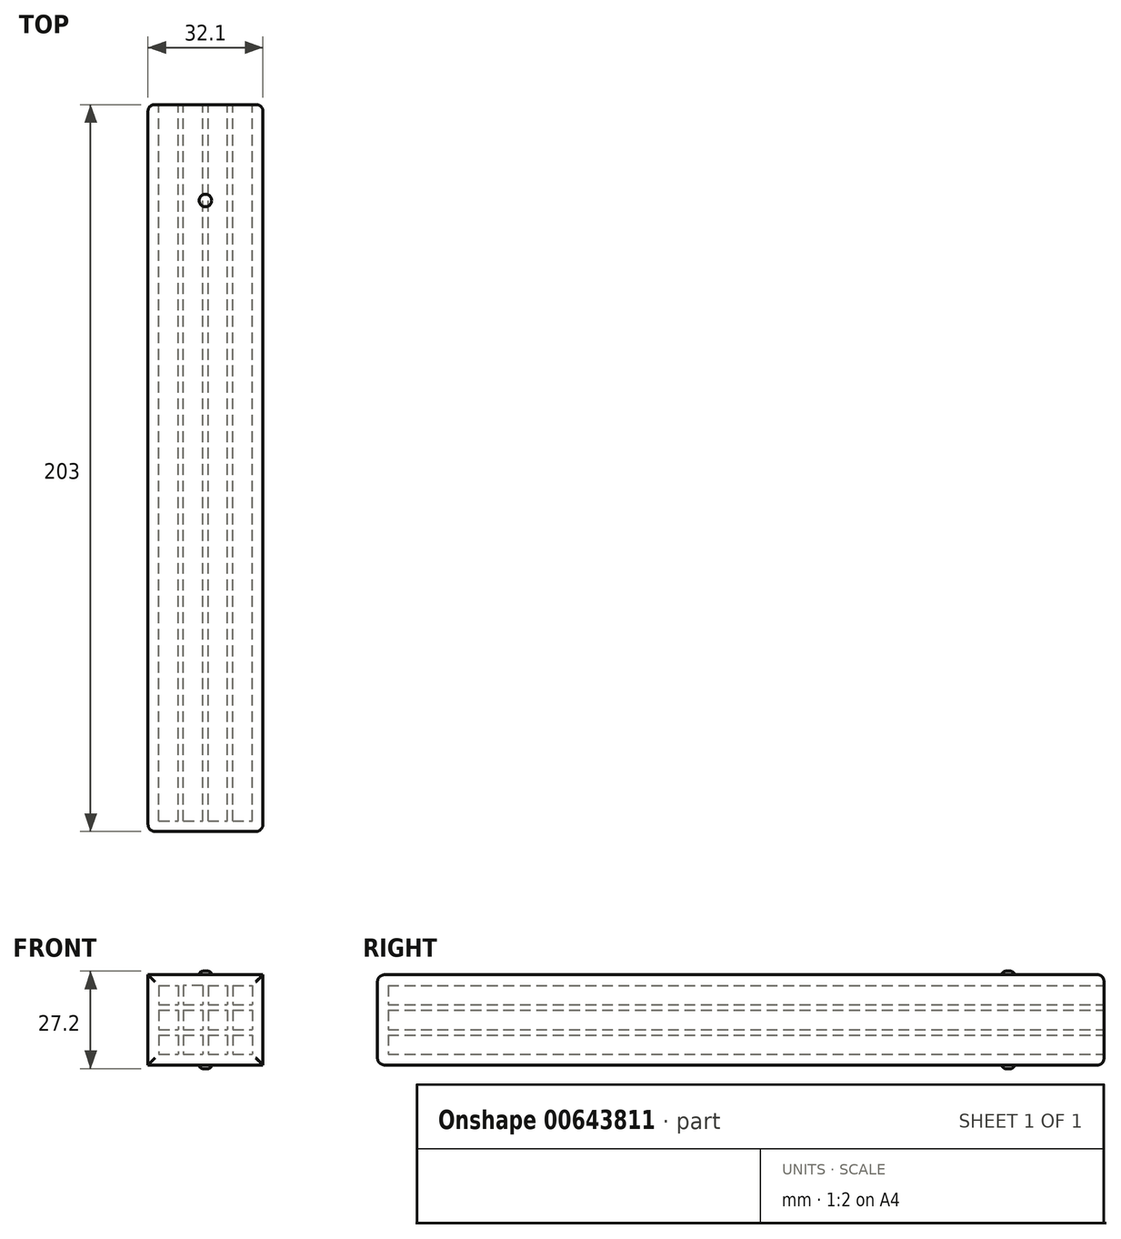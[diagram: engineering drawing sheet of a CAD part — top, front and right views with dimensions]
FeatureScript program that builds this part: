
annotation { "Feature Type Name" : "Feature", "Feature Type Description" : "" }
export const myFeature = defineFeature(function(context is Context, id is Id, definition is map)
    precondition{}
    {
        {
            var Q0;
            Q0=qCreatedBy(makeId("Front.planeOp"),FACE);
            var sketch = newSketch(context, id + "F0", { "sketchPlane" : qUnion([Q0])});
            skLineSegment(sketch, "E0.top", {"start": v(-16.76, 12.2) * mm, "end": v(15.34, 12.2) * mm});
            skLineSegment(sketch, "E0.left", {"start": v(-16.76, -13) * mm, "end": v(-16.76, 12.2) * mm});
            skLineSegment(sketch, "E1.0", {"start": v(-13.76, 9.2) * mm, "end": v(-8.01, 9.2) * mm});
            skLineSegment(sketch, "E2.bottom", {"start": v(-13.76, 9.2) * mm, "end": v(-8.36, 9.2) * mm});
            skLineSegment(sketch, "E2.left", {"start": v(-4.86, 32.02) * mm, "end": v(-4.86, 32.02) * mm});
            skLineSegment(sketch, "E3.bottom", {"start": v(-1.46, 9.2) * mm, "end": v(-6.86, 9.2) * mm});
            skLineSegment(sketch, "E4.left", {"start": v(-13.76, 0.75) * mm, "end": v(-13.76, -3.1) * mm});
            skLineSegment(sketch, "E5.left", {"start": v(-13.76, 9.2) * mm, "end": v(-13.76, 3.8) * mm});
            skLineSegment(sketch, "E6", {"start": v(-8.36, 9.2) * mm, "end": v(-8.36, 3.8) * mm});
            skLineSegment(sketch, "E7", {"start": v(-6.86, 9.2) * mm, "end": v(-6.86, 3.8) * mm});
            skLineSegment(sketch, "E8", {"start": v(-1.46, 9.2) * mm, "end": v(-1.46, 3.8) * mm});
            skLineSegment(sketch, "E9", {"start": v(0.04, 9.2) * mm, "end": v(0.04, 3.8) * mm});
            skLineSegment(sketch, "E10", {"start": v(5.44, 9.2) * mm, "end": v(5.44, 3.8) * mm});
            skLineSegment(sketch, "E11", {"start": v(6.94, 9.2) * mm, "end": v(6.94, 3.8) * mm});
            skLineSegment(sketch, "E12", {"start": v(-13.76, 3.8) * mm, "end": v(-8.36, 3.8) * mm});
            skLineSegment(sketch, "E13", {"start": v(-13.76, 2.3) * mm, "end": v(-8.36, 2.3) * mm});
            skLineSegment(sketch, "E14", {"start": v(-13.76, -3.1) * mm, "end": v(-8.36, -3.1) * mm});
            skLineSegment(sketch, "E15", {"start": v(12.34, 9.2) * mm, "end": v(12.34, 3.8) * mm});
            skLineSegment(sketch, "E16", {"start": v(15.34, 12.2) * mm, "end": v(15.34, -13) * mm});
            skPoint(sketch, "E17.orphan", {"position": v(13.24, 9.2) * mm});
            skPoint(sketch, "E18.orphan", {"position": v(13.24, 3.8) * mm});
            skPoint(sketch, "E19.orphan", {"position": v(13.24, 2.3) * mm});
            skPoint(sketch, "E20.orphan", {"position": v(13.24, -2.88) * mm});
            skPoint(sketch, "E21.orphan", {"position": v(13.24, -9.45) * mm});
            skLineSegment(sketch, "E22.0", {"start": v(-13.76, -4.6) * mm, "end": v(-8.36, -4.6) * mm});
            skLineSegment(sketch, "E23.0", {"start": v(-13.76, -10) * mm, "end": v(-8.36, -10) * mm});
            skLineSegment(sketch, "E24.trimOffspring", {"start": v(6.94, -10) * mm, "end": v(12.34, -10) * mm});
            skLineSegment(sketch, "E25.trimOffspring", {"start": v(6.94, -4.6) * mm, "end": v(12.34, -4.6) * mm});
            skLineSegment(sketch, "E26.trimOffspring", {"start": v(5.44, -4.6) * mm, "end": v(5.44, -10) * mm});
            skLineSegment(sketch, "E27.trimOffspring", {"start": v(6.94, -3.1) * mm, "end": v(12.34, -3.1) * mm});
            skLineSegment(sketch, "E28.trimOffspring", {"start": v(6.94, -4.6) * mm, "end": v(6.94, -10) * mm});
            skLineSegment(sketch, "E29.trimOffspring", {"start": v(12.34, -4.6) * mm, "end": v(12.34, -10) * mm});
            skLineSegment(sketch, "E30.trimOffspring", {"start": v(12.34, 2.3) * mm, "end": v(12.34, -3.1) * mm});
            skLineSegment(sketch, "E31.trimOffspring", {"start": v(6.94, 2.3) * mm, "end": v(6.94, -3.1) * mm});
            skLineSegment(sketch, "E32.trimOffspring", {"start": v(5.44, 2.3) * mm, "end": v(5.44, -3.1) * mm});
            skLineSegment(sketch, "E33.trimOffspring", {"start": v(6.94, 3.8) * mm, "end": v(12.34, 3.8) * mm});
            skLineSegment(sketch, "E34.trimOffspring", {"start": v(6.94, 2.3) * mm, "end": v(12.34, 2.3) * mm});
            skLineSegment(sketch, "E35.trimOffspring", {"start": v(0.04, -10) * mm, "end": v(5.44, -10) * mm});
            skLineSegment(sketch, "E36.trimOffspring", {"start": v(-6.86, 9.2) * mm, "end": v(-1.46, 9.2) * mm});
            skLineSegment(sketch, "E37.trimOffspring", {"start": v(-6.86, 3.8) * mm, "end": v(-1.46, 3.8) * mm});
            skLineSegment(sketch, "E38.trimOffspring", {"start": v(-6.86, 2.3) * mm, "end": v(-1.46, 2.3) * mm});
            skLineSegment(sketch, "E39.trimOffspring", {"start": v(-8.36, 2.3) * mm, "end": v(-8.36, -3.1) * mm});
            skLineSegment(sketch, "E40.trimOffspring", {"start": v(-6.86, 2.3) * mm, "end": v(-6.86, -3.1) * mm});
            skLineSegment(sketch, "E41.trimOffspring", {"start": v(-13.76, 3.8) * mm, "end": v(-13.76, 9.2) * mm});
            skLineSegment(sketch, "E42.trimOffspring", {"start": v(-13.76, -4.6) * mm, "end": v(-13.76, -6.95) * mm});
            skLineSegment(sketch, "E43.trimOffspring", {"start": v(-8.36, -4.6) * mm, "end": v(-8.36, -10) * mm});
            skLineSegment(sketch, "E44.trimOffspring", {"start": v(-6.86, -3.1) * mm, "end": v(-1.46, -3.1) * mm});
            skLineSegment(sketch, "E45.trimOffspring", {"start": v(-6.86, -4.6) * mm, "end": v(-6.86, -10) * mm});
            skLineSegment(sketch, "E46.trimOffspring", {"start": v(-6.86, -4.6) * mm, "end": v(-1.46, -4.6) * mm});
            skLineSegment(sketch, "E47.trimOffspring", {"start": v(-1.46, -4.6) * mm, "end": v(-1.46, -10) * mm});
            skLineSegment(sketch, "E48.trimOffspring", {"start": v(0.04, -3.1) * mm, "end": v(5.44, -3.1) * mm});
            skLineSegment(sketch, "E49.trimOffspring", {"start": v(0.04, -4.6) * mm, "end": v(0.04, -10) * mm});
            skLineSegment(sketch, "E50.trimOffspring", {"start": v(0.04, -4.6) * mm, "end": v(5.44, -4.6) * mm});
            skLineSegment(sketch, "E51.trimOffspring", {"start": v(-6.86, -10) * mm, "end": v(-1.46, -10) * mm});
            skLineSegment(sketch, "E52.trimOffspring", {"start": v(-13.76, -10) * mm, "end": v(-13.76, 2.3) * mm});
            skLineSegment(sketch, "E53.trimOffspring", {"start": v(0.04, 2.3) * mm, "end": v(5.44, 2.3) * mm});
            skLineSegment(sketch, "E54.trimOffspring", {"start": v(0.04, 3.8) * mm, "end": v(5.44, 3.8) * mm});
            skLineSegment(sketch, "E55.trimOffspring", {"start": v(-1.46, 2.3) * mm, "end": v(-1.46, -3.1) * mm});
            skLineSegment(sketch, "E56.trimOffspring", {"start": v(0.04, 2.3) * mm, "end": v(0.04, -3.1) * mm});
            skPoint(sketch, "E57.orphan", {"position": v(-0.26, 9.2) * mm});
            skLineSegment(sketch, "E58.trimOffspring", {"start": v(0.04, 9.2) * mm, "end": v(5.44, 9.2) * mm});
            skLineSegment(sketch, "E59.trimOffspring", {"start": v(6.94, 9.2) * mm, "end": v(12.34, 9.2) * mm});
            skLineSegment(sketch, "E60", {"start": v(-16.76, -13) * mm, "end": v(15.34, -13) * mm});
            skSolve(sketch);
        }
        {
            var Q0;
            Q0=makeQuery(id+"F0.imprint","IMPRINT",FACE,{"disambiguationData":[TD([[makeQuery(id+"F0.imprint","IMPRINT",EDGE,{"derivedFrom":sQuery(id+"F0.wireOp",EDGE,"E0.top")}),-1.0]])]});
            extrude(context, id + "F1", {"entities" : qUnion([Q0]), "depth" : 200 * mm, "offsetDistance" : 25 * mm});
        }
        {
            var Q0;
            Q0=makeQuery(id+"F1.opExtrude","CAP_FACE",FACE,{"disambiguationData":[OSD([sQuery(id+"F0.wireOp",EDGE,"E0.top"),sQuery(id+"F0.wireOp",EDGE,"E0.left"),sQuery(id+"F0.wireOp",EDGE,"E1.0"),sQuery(id+"F0.wireOp",EDGE,"E6"),sQuery(id+"F0.wireOp",EDGE,"E7"),sQuery(id+"F0.wireOp",EDGE,"E8"),sQuery(id+"F0.wireOp",EDGE,"E9"),sQuery(id+"F0.wireOp",EDGE,"E10"),sQuery(id+"F0.wireOp",EDGE,"E11"),sQuery(id+"F0.wireOp",EDGE,"E12"),sQuery(id+"F0.wireOp",EDGE,"E13"),sQuery(id+"F0.wireOp",EDGE,"E14"),sQuery(id+"F0.wireOp",EDGE,"E15"),sQuery(id+"F0.wireOp",EDGE,"E16"),sQuery(id+"F0.wireOp",EDGE,"E22.0"),sQuery(id+"F0.wireOp",EDGE,"E23.0"),sQuery(id+"F0.wireOp",EDGE,"E24.trimOffspring"),sQuery(id+"F0.wireOp",EDGE,"E25.trimOffspring"),sQuery(id+"F0.wireOp",EDGE,"E26.trimOffspring"),sQuery(id+"F0.wireOp",EDGE,"E27.trimOffspring"),sQuery(id+"F0.wireOp",EDGE,"E28.trimOffspring"),sQuery(id+"F0.wireOp",EDGE,"E29.trimOffspring"),sQuery(id+"F0.wireOp",EDGE,"E30.trimOffspring"),sQuery(id+"F0.wireOp",EDGE,"E31.trimOffspring"),sQuery(id+"F0.wireOp",EDGE,"E32.trimOffspring"),sQuery(id+"F0.wireOp",EDGE,"E33.trimOffspring"),sQuery(id+"F0.wireOp",EDGE,"E34.trimOffspring"),sQuery(id+"F0.wireOp",EDGE,"E35.trimOffspring"),sQuery(id+"F0.wireOp",EDGE,"E36.trimOffspring"),sQuery(id+"F0.wireOp",EDGE,"E37.trimOffspring"),sQuery(id+"F0.wireOp",EDGE,"E38.trimOffspring"),sQuery(id+"F0.wireOp",EDGE,"E39.trimOffspring"),sQuery(id+"F0.wireOp",EDGE,"E40.trimOffspring"),sQuery(id+"F0.wireOp",EDGE,"E41.trimOffspring"),sQuery(id+"F0.wireOp",EDGE,"E43.trimOffspring"),sQuery(id+"F0.wireOp",EDGE,"E44.trimOffspring"),sQuery(id+"F0.wireOp",EDGE,"E45.trimOffspring"),sQuery(id+"F0.wireOp",EDGE,"E46.trimOffspring"),sQuery(id+"F0.wireOp",EDGE,"E47.trimOffspring"),sQuery(id+"F0.wireOp",EDGE,"E48.trimOffspring"),sQuery(id+"F0.wireOp",EDGE,"E49.trimOffspring"),sQuery(id+"F0.wireOp",EDGE,"E50.trimOffspring"),sQuery(id+"F0.wireOp",EDGE,"E51.trimOffspring"),sQuery(id+"F0.wireOp",EDGE,"E52.trimOffspring"),sQuery(id+"F0.wireOp",EDGE,"E53.trimOffspring"),sQuery(id+"F0.wireOp",EDGE,"E54.trimOffspring"),sQuery(id+"F0.wireOp",EDGE,"E55.trimOffspring"),sQuery(id+"F0.wireOp",EDGE,"E56.trimOffspring"),sQuery(id+"F0.wireOp",EDGE,"E58.trimOffspring"),sQuery(id+"F0.wireOp",EDGE,"E59.trimOffspring"),sQuery(id+"F0.wireOp",EDGE,"E60")])],"isStart":false});
            var sketch = newSketch(context, id + "F2", { "sketchPlane" : qUnion([Q0])});
            skSolve(sketch);
        }
        {
            var Q0;
            Q0=makeQuery(id+"F2.imprint","IMPRINT",FACE,{"disambiguationData":[TD([[makeQuery(id+"F2.imprint","IMPRINT",EDGE,{"derivedFrom":makeQuery(id+"F1.opExtrude","CAP_EDGE",EDGE,{"disambiguationData":[OSD([sQuery(id+"F0.wireOp",EDGE,"E0.top")])],"isStart":false})}),-1.0]])]});
            var sketch = newSketch(context, id + "F3", { "sketchPlane" : qUnion([Q0])});
            skPoint(sketch, "E61.0", {"position": v(-16.76, 12.2) * mm});
            skPoint(sketch, "E62.0", {"position": v(15.34, -13) * mm});
            skLineSegment(sketch, "E63.bottom", {"start": v(-16.76, 12.2) * mm, "end": v(15.34, 12.2) * mm});
            skLineSegment(sketch, "E63.top", {"start": v(-16.76, -13) * mm, "end": v(15.34, -13) * mm});
            skLineSegment(sketch, "E63.left", {"start": v(-16.76, 12.2) * mm, "end": v(-16.76, -13) * mm});
            skLineSegment(sketch, "E63.right", {"start": v(15.34, 12.2) * mm, "end": v(15.34, -13) * mm});
            skSolve(sketch);
        }
        {
            var Q0;
            Q0 = qSketchRegion(id + "F3", true);
            extrude(context, id + "F4", {"entities" : qUnion([Q0]), "operationType" : NewBodyOperationType.ADD, "depth" : 3 * mm, "offsetDistance" : 25 * mm});
        }
        {
            var Q0;
            Q0=makeQuery(id+"F4.opExtrude","CAP_EDGE",EDGE,{"disambiguationData":[OSD([sQuery(id+"F3.wireOp",EDGE,"E63.right")])],"isStart":false});
            var Q1;
            Q1=makeQuery(id+"F4.opExtrude","CAP_FACE",FACE,{"disambiguationData":[OSD([sQuery(id+"F3.wireOp",EDGE,"E63.bottom"),sQuery(id+"F3.wireOp",EDGE,"E63.top"),sQuery(id+"F3.wireOp",EDGE,"E63.left"),sQuery(id+"F3.wireOp",EDGE,"E63.right")])],"isStart":false});
            fillet(context, id + "F5", {"entities" : qUnion([Q0, Q1]), "radius" : 2 * mm, "tangentPropagation" : true, "allowEdgeOverflow" : false});
        }
        {
            var Q0;
            Q0=makeQuery(id+"F1.opExtrude","CAP_EDGE",EDGE,{"disambiguationData":[OSD([sQuery(id+"F0.wireOp",EDGE,"E0.top")])],"isStart":true});
            var Q1;
            Q1=makeQuery(id+"F1.opExtrude","CAP_EDGE",EDGE,{"disambiguationData":[OSD([sQuery(id+"F0.wireOp",EDGE,"E16")])],"isStart":true});
            var Q2;
            Q2=makeQuery(id+"F1.opExtrude","CAP_EDGE",EDGE,{"disambiguationData":[OSD([sQuery(id+"F0.wireOp",EDGE,"E60")])],"isStart":true});
            var Q3;
            Q3=makeQuery(id+"F1.opExtrude","CAP_EDGE",EDGE,{"disambiguationData":[OSD([sQuery(id+"F0.wireOp",EDGE,"E0.left")])],"isStart":true});
            fillet(context, id + "F6", {"entities" : qUnion([Q0, Q1, Q2, Q3]), "radius" : 1.75 * mm, "tangentPropagation" : true, "allowEdgeOverflow" : false});
        }
        {
            var Q0;
            Q0=makeQuery(id+"F4.boolean.opBoolean","MERGE",FACE,{"derivedFrom":[makeQuery(id+"F1.opExtrude","SWEPT_FACE",FACE,{"disambiguationData":[OSD([sQuery(id+"F0.wireOp",EDGE,"E0.top")])]}),makeQuery(id+"F4.opExtrude","SWEPT_FACE",FACE,{"disambiguationData":[OSD([sQuery(id+"F3.wireOp",EDGE,"E63.bottom")])]})]});
            var sketch = newSketch(context, id + "F7", { "sketchPlane" : qUnion([Q0])});
            skPoint(sketch, "E64.0", {"position": v(-0.71, -1.75) * mm});
            skLineSegment(sketch, "E65", {"start": v(-0.71, -1.75) * mm, "end": v(-0.71, -21.54) * mm, "construction": true});
            skCircle(sketch, "E66", {"center": v(-0.71, -26.75) * mm, "radius": 1.75 * mm});
            skSolve(sketch);
        }
        {
            var Q0;
            Q0 = qSketchRegion(id + "F7", true);
            extrude(context, id + "F8", {"entities" : qUnion([Q0]), "operationType" : NewBodyOperationType.ADD, "depth" : 1 * mm, "offsetDistance" : 25 * mm});
        }
        {
            var Q0;
            Q0=makeQuery(id+"F8.opExtrude","CAP_EDGE",EDGE,{"disambiguationData":[OSD([sQuery(id+"F7.wireOp",EDGE,"E66")])],"isStart":false});
            fillet(context, id + "F9", {"entities" : qUnion([Q0]), "radius" : 1 * mm, "tangentPropagation" : true, "allowEdgeOverflow" : false});
        }
        {
            var Q0;
            Q0=makeQuery(id+"F4.boolean.opBoolean","MERGE",FACE,{"derivedFrom":[makeQuery(id+"F1.opExtrude","SWEPT_FACE",FACE,{"disambiguationData":[OSD([sQuery(id+"F0.wireOp",EDGE,"E60")])]}),makeQuery(id+"F4.opExtrude","SWEPT_FACE",FACE,{"disambiguationData":[OSD([sQuery(id+"F3.wireOp",EDGE,"E63.top")])]})]});
            var sketch = newSketch(context, id + "F10", { "sketchPlane" : qUnion([Q0])});
            skCircle(sketch, "E67.0", {"center": v(-0.71, 26.75) * mm, "radius": 1.75 * mm});
            skSolve(sketch);
        }
        {
            var Q0;
            Q0 = qSketchRegion(id + "F10", true);
            extrude(context, id + "F11", {"entities" : qUnion([Q0]), "operationType" : NewBodyOperationType.ADD, "depth" : 1 * mm, "offsetDistance" : 25 * mm});
        }
        {
            var Q0;
            Q0=makeQuery(id+"F11.opExtrude","CAP_EDGE",EDGE,{"disambiguationData":[OSD([sQuery(id+"F10.wireOp",EDGE,"E67.0")])],"isStart":false});
            fillet(context, id + "F12", {"entities" : qUnion([Q0]), "radius" : 1 * mm, "tangentPropagation" : true, "allowEdgeOverflow" : false});
        }
    });
